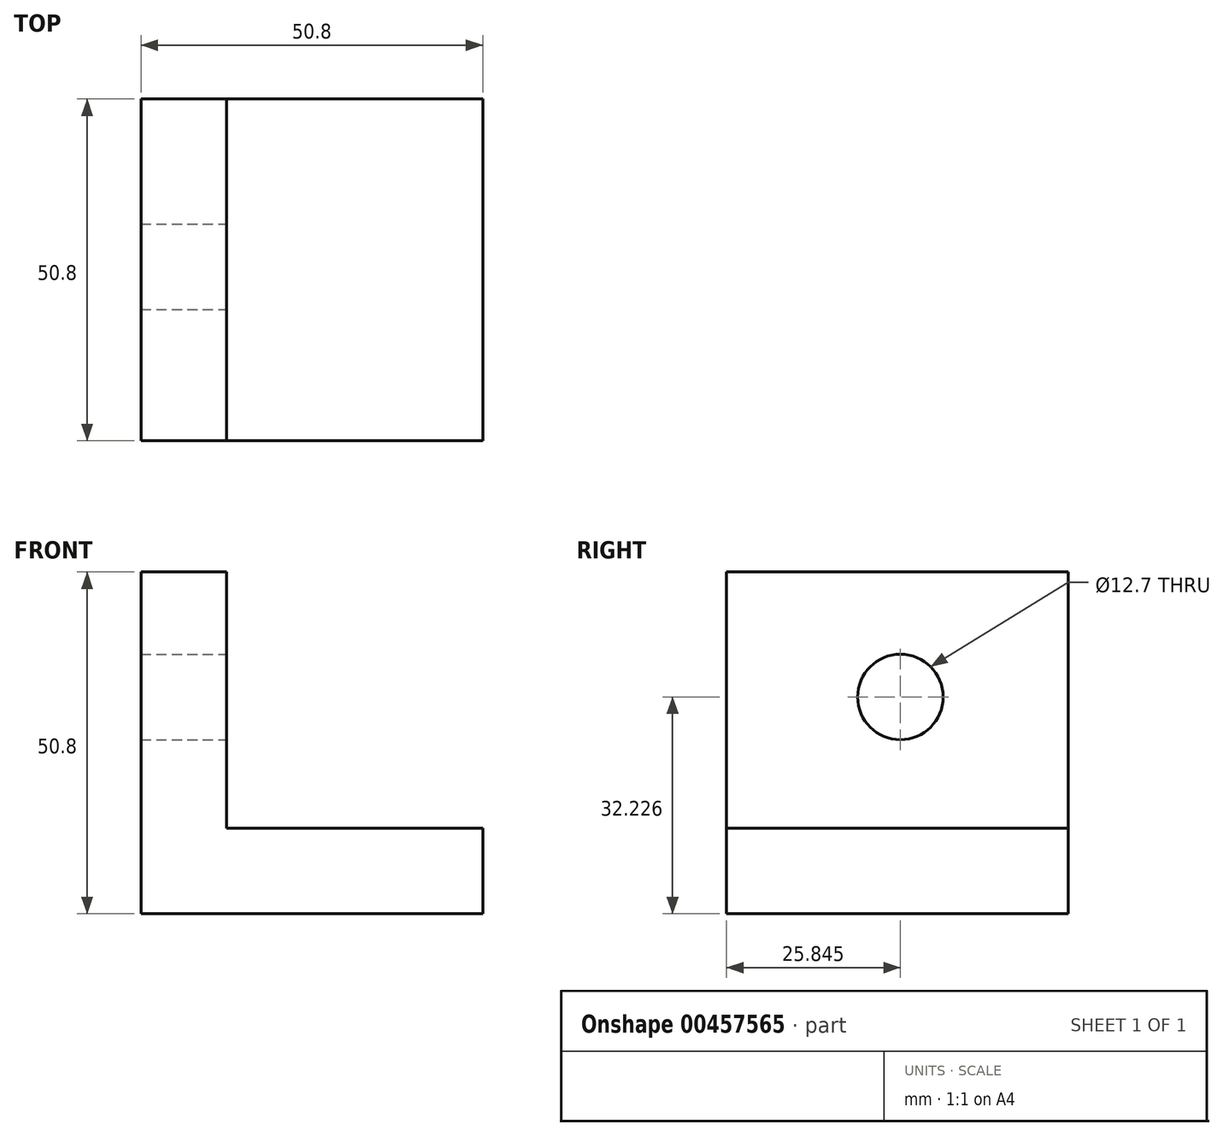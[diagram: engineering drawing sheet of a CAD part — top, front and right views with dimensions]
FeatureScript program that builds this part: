
annotation { "Feature Type Name" : "Feature", "Feature Type Description" : "" }
export const myFeature = defineFeature(function(context is Context, id is Id, definition is map)
    precondition{}
    {
        {
            var Q0;
            Q0=qCreatedBy(makeId("Top.planeOp"),FACE);
            var sketch = newSketch(context, id + "F0", { "sketchPlane" : qUnion([Q0])});
            skLineSegment(sketch, "E0.bottom", {"start": v(-32.17, 40.3) * mm, "end": v(18.63, 40.3) * mm});
            skLineSegment(sketch, "E0.top", {"start": v(-32.17, -10.5) * mm, "end": v(18.63, -10.5) * mm});
            skLineSegment(sketch, "E0.left", {"start": v(-32.17, 40.3) * mm, "end": v(-32.17, -10.5) * mm});
            skLineSegment(sketch, "E0.right", {"start": v(18.63, 40.3) * mm, "end": v(18.63, -10.5) * mm});
            skSolve(sketch);
        }
        {
            var Q0;
            Q0=makeQuery(id+"F0.imprint","IMPRINT",FACE,{"disambiguationData":[TD([[makeQuery(id+"F0.imprint","IMPRINT",EDGE,{"derivedFrom":sQuery(id+"F0.wireOp",EDGE,"E0.bottom")}),-1.0]])]});
            extrude(context, id + "F1", {"entities" : qUnion([Q0]), "depth" : 12.7 * mm});
        }
        {
            var Q0;
            Q0=makeQuery(id+"F1.opExtrude","CAP_FACE",FACE,{"disambiguationData":[OSD([sQuery(id+"F0.wireOp",EDGE,"E0.bottom"),sQuery(id+"F0.wireOp",EDGE,"E0.top"),sQuery(id+"F0.wireOp",EDGE,"E0.left"),sQuery(id+"F0.wireOp",EDGE,"E0.right")])],"isStart":false});
            var sketch = newSketch(context, id + "F2", { "sketchPlane" : qUnion([Q0])});
            skLineSegment(sketch, "E1.bottom", {"start": v(-32.17, 40.3) * mm, "end": v(-19.47, 40.3) * mm});
            skLineSegment(sketch, "E1.top", {"start": v(-32.17, -10.5) * mm, "end": v(-19.47, -10.5) * mm});
            skLineSegment(sketch, "E1.left", {"start": v(-32.17, 40.3) * mm, "end": v(-32.17, -10.5) * mm});
            skLineSegment(sketch, "E1.right", {"start": v(-19.47, 40.3) * mm, "end": v(-19.47, -10.5) * mm});
            skSolve(sketch);
        }
        {
            var Q0;
            Q0=makeQuery(id+"F2.imprint","IMPRINT",FACE,{"disambiguationData":[TD([[makeQuery(id+"F2.imprint","IMPRINT",EDGE,{"derivedFrom":sQuery(id+"F2.wireOp",EDGE,"E1.bottom")}),-1.0]])]});
            extrude(context, id + "F3", {"entities" : qUnion([Q0]), "operationType" : NewBodyOperationType.ADD, "depth" : 38.1 * mm});
        }
        {
            var Q0;
            Q0=makeQuery(id+"F3.opExtrude","SWEPT_FACE",FACE,{"disambiguationData":[OSD([sQuery(id+"F2.wireOp",EDGE,"E1.right")])]});
            var sketch = newSketch(context, id + "F4", { "sketchPlane" : qUnion([Q0])});
            skCircle(sketch, "E2", {"center": v(15.34, 32.23) * mm, "radius": 6.35 * mm});
            skSolve(sketch);
        }
        {
            var Q0;
            Q0=makeQuery(id+"F4.imprint","IMPRINT",FACE,{"disambiguationData":[TD([[makeQuery(id+"F4.imprint","IMPRINT",EDGE,{"derivedFrom":sQuery(id+"F4.wireOp",EDGE,"E2")}),1.0]])]});
            extrude(context, id + "F5", {"entities" : qUnion([Q0]), "operationType" : NewBodyOperationType.REMOVE, "oppositeDirection" : true, "depth" : 25.4 * mm});
        }
    });
